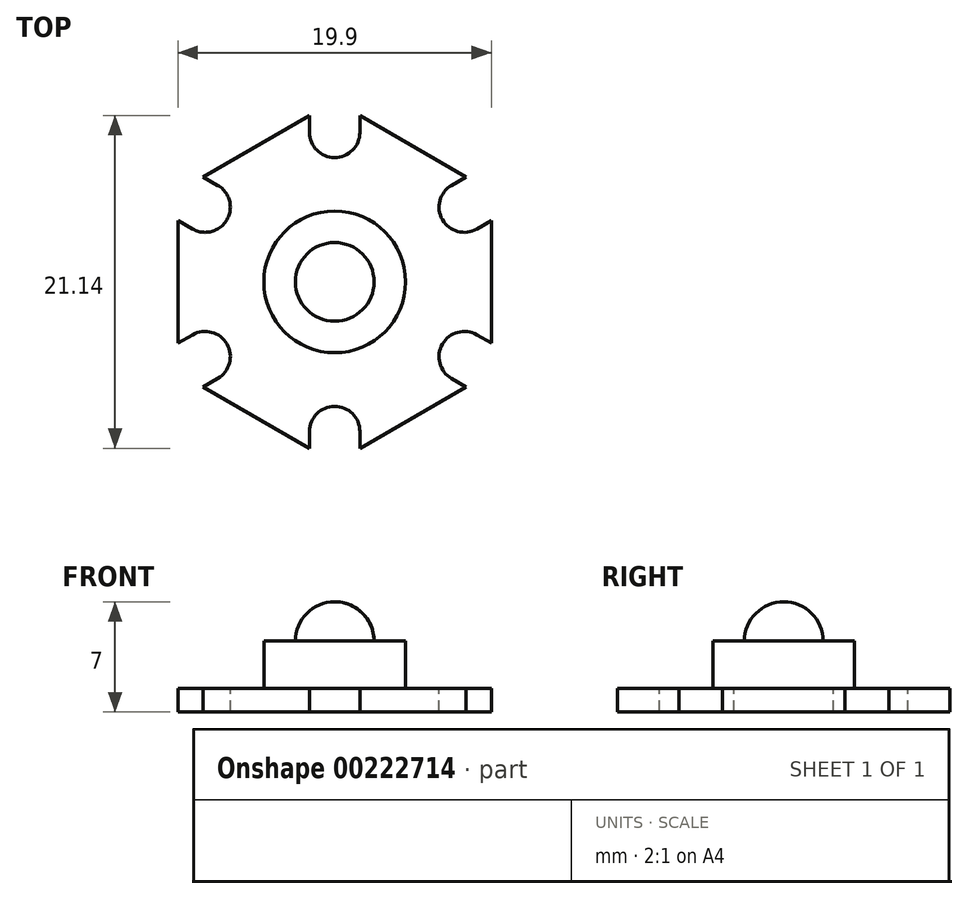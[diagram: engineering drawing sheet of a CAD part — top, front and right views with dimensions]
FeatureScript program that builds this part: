
annotation { "Feature Type Name" : "Feature", "Feature Type Description" : "" }
export const myFeature = defineFeature(function(context is Context, id is Id, definition is map)
    precondition{}
    {
        {
            var Q0;
            Q0=qCreatedBy(makeId("Top.planeOp"),FACE);
            var sketch = newSketch(context, id + "F0", { "sketchPlane" : qUnion([Q0])});
            skCircle(sketch, "E0.cCircle", {"center": v(0, 0) * mm, "radius": 9.95 * mm, "construction": true});
            skLineSegment(sketch, "E0.0", {"start": v(9.95, 5.74) * mm, "end": v(9.95, -5.74) * mm});
            skLineSegment(sketch, "E0.1", {"start": v(9.95, -5.74) * mm, "end": v(0, -11.49) * mm});
            skLineSegment(sketch, "E0.2", {"start": v(0, -11.49) * mm, "end": v(-9.95, -5.74) * mm});
            skLineSegment(sketch, "E0.3", {"start": v(-9.95, -5.74) * mm, "end": v(-9.95, 5.74) * mm});
            skLineSegment(sketch, "E0.4", {"start": v(-9.95, 5.74) * mm, "end": v(0, 11.49) * mm});
            skLineSegment(sketch, "E0.5", {"start": v(0, 11.49) * mm, "end": v(9.95, 5.74) * mm});
            skPoint(sketch, "E0.0.midPoint", {"position": v(9.95, 0) * mm});
            skSolve(sketch);
        }
        {
            var Q0;
            Q0=makeQuery(id+"F0.imprint","IMPRINT",FACE,{"disambiguationData":[TD([[makeQuery(id+"F0.imprint","IMPRINT",EDGE,{"derivedFrom":sQuery(id+"F0.wireOp",EDGE,"E0.0")}),-1.0]])]});
            extrude(context, id + "F1", {"entities" : qUnion([Q0]), "depth" : 1.5 * mm});
        }
        {
            var Q0;
            Q0=makeQuery(id+"F1.opExtrude","CAP_FACE",FACE,{"disambiguationData":[OSD([sQuery(id+"F0.wireOp",EDGE,"E0.0"),sQuery(id+"F0.wireOp",EDGE,"E0.1"),sQuery(id+"F0.wireOp",EDGE,"E0.2"),sQuery(id+"F0.wireOp",EDGE,"E0.3"),sQuery(id+"F0.wireOp",EDGE,"E0.4"),sQuery(id+"F0.wireOp",EDGE,"E0.5")])],"isStart":false});
            var sketch = newSketch(context, id + "F2", { "sketchPlane" : qUnion([Q0])});
            skLineSegment(sketch, "E1.0.0", {"start": v(9.95, 5.74) * mm, "end": v(0, 11.49) * mm, "construction": true});
            skLineSegment(sketch, "E1.0.1", {"start": v(0, 11.49) * mm, "end": v(-9.95, 5.74) * mm, "construction": true});
            skLineSegment(sketch, "E1.0.2", {"start": v(-9.95, 5.74) * mm, "end": v(-9.95, -5.74) * mm, "construction": true});
            skLineSegment(sketch, "E1.0.3", {"start": v(-9.95, -5.74) * mm, "end": v(0, -11.49) * mm, "construction": true});
            skLineSegment(sketch, "E1.0.4", {"start": v(0, -11.49) * mm, "end": v(9.95, -5.74) * mm, "construction": true});
            skLineSegment(sketch, "E1.0.5", {"start": v(9.95, -5.74) * mm, "end": v(9.95, 5.74) * mm, "construction": true});
            skLineSegment(sketch, "E2", {"start": v(0, 11.49) * mm, "end": v(0, -11.49) * mm, "construction": true});
            skArc(sketch, "E3", {"start": v(-1.6, 9.5) * mm, "mid": v(0, 7.9) * mm, "end": v(1.6, 9.5) * mm});
            skLineSegment(sketch, "E4", {"start": v(-1.6, 9.5) * mm, "end": v(1.6, 9.5) * mm, "construction": true});
            skLineSegment(sketch, "E5", {"start": v(-1.6, 9.5) * mm, "end": v(-1.6, 10.57) * mm});
            skLineSegment(sketch, "E6", {"start": v(1.6, 9.5) * mm, "end": v(1.6, 10.57) * mm});
            skLineSegment(sketch, "E7", {"start": v(-1.6, 10.57) * mm, "end": v(0, 11.49) * mm});
            skLineSegment(sketch, "E8", {"start": v(1.6, 10.57) * mm, "end": v(0, 11.49) * mm});
            skLineSegment(sketch, "E9.1.0", {"start": v(-7.43, 6.14) * mm, "end": v(-8.35, 6.67) * mm});
            skLineSegment(sketch, "E9.1.1", {"start": v(-9.03, 3.36) * mm, "end": v(-9.95, 3.9) * mm});
            skLineSegment(sketch, "E9.1.2", {"start": v(-9.03, 3.36) * mm, "end": v(-7.43, 6.14) * mm, "construction": true});
            skLineSegment(sketch, "E9.1.3", {"start": v(-8.35, 6.67) * mm, "end": v(-9.95, 5.74) * mm});
            skArc(sketch, "E9.1.4", {"start": v(-9.03, 3.36) * mm, "mid": v(-6.84, 3.95) * mm, "end": v(-7.43, 6.14) * mm});
            skLineSegment(sketch, "E9.1.5", {"start": v(-9.95, 3.9) * mm, "end": v(-9.95, 5.74) * mm});
            skLineSegment(sketch, "E9.2.0", {"start": v(-9.03, -3.36) * mm, "end": v(-9.95, -3.9) * mm});
            skLineSegment(sketch, "E9.2.1", {"start": v(-7.43, -6.14) * mm, "end": v(-8.35, -6.67) * mm});
            skLineSegment(sketch, "E9.2.2", {"start": v(-7.43, -6.14) * mm, "end": v(-9.03, -3.36) * mm, "construction": true});
            skLineSegment(sketch, "E9.2.3", {"start": v(-9.95, -3.9) * mm, "end": v(-9.95, -5.74) * mm});
            skArc(sketch, "E9.2.4", {"start": v(-7.43, -6.14) * mm, "mid": v(-6.84, -3.95) * mm, "end": v(-9.03, -3.36) * mm});
            skLineSegment(sketch, "E9.2.5", {"start": v(-8.35, -6.67) * mm, "end": v(-9.95, -5.74) * mm});
            skLineSegment(sketch, "E9.3.0", {"start": v(-1.6, -9.5) * mm, "end": v(-1.6, -10.57) * mm});
            skLineSegment(sketch, "E9.3.1", {"start": v(1.6, -9.5) * mm, "end": v(1.6, -10.57) * mm});
            skLineSegment(sketch, "E9.3.2", {"start": v(1.6, -9.5) * mm, "end": v(-1.6, -9.5) * mm, "construction": true});
            skLineSegment(sketch, "E9.3.3", {"start": v(-1.6, -10.57) * mm, "end": v(0, -11.49) * mm});
            skArc(sketch, "E9.3.4", {"start": v(1.6, -9.5) * mm, "mid": v(0, -7.9) * mm, "end": v(-1.6, -9.5) * mm});
            skLineSegment(sketch, "E9.3.5", {"start": v(1.6, -10.57) * mm, "end": v(0, -11.49) * mm});
            skLineSegment(sketch, "E9.4.0", {"start": v(7.43, -6.14) * mm, "end": v(8.35, -6.67) * mm});
            skLineSegment(sketch, "E9.4.1", {"start": v(9.03, -3.36) * mm, "end": v(9.95, -3.9) * mm});
            skLineSegment(sketch, "E9.4.2", {"start": v(9.03, -3.36) * mm, "end": v(7.43, -6.14) * mm, "construction": true});
            skLineSegment(sketch, "E9.4.3", {"start": v(8.35, -6.67) * mm, "end": v(9.95, -5.74) * mm});
            skArc(sketch, "E9.4.4", {"start": v(9.03, -3.36) * mm, "mid": v(6.84, -3.95) * mm, "end": v(7.43, -6.14) * mm});
            skLineSegment(sketch, "E9.4.5", {"start": v(9.95, -3.9) * mm, "end": v(9.95, -5.74) * mm});
            skLineSegment(sketch, "E9.5.0", {"start": v(9.03, 3.36) * mm, "end": v(9.95, 3.9) * mm});
            skLineSegment(sketch, "E9.5.1", {"start": v(7.43, 6.14) * mm, "end": v(8.35, 6.67) * mm});
            skLineSegment(sketch, "E9.5.2", {"start": v(7.43, 6.14) * mm, "end": v(9.03, 3.36) * mm, "construction": true});
            skLineSegment(sketch, "E9.5.3", {"start": v(9.95, 3.9) * mm, "end": v(9.95, 5.74) * mm});
            skArc(sketch, "E9.5.4", {"start": v(7.43, 6.14) * mm, "mid": v(6.84, 3.95) * mm, "end": v(9.03, 3.36) * mm});
            skLineSegment(sketch, "E9.5.5", {"start": v(8.35, 6.67) * mm, "end": v(9.95, 5.74) * mm});
            skPoint(sketch, "E9.center", {"position": v(0, 0) * mm});
            skSolve(sketch);
        }
        {
            var Q0;
            Q0=makeQuery(id+"F2.imprint","IMPRINT",FACE,{"disambiguationData":[TD([[makeQuery(id+"F2.imprint","IMPRINT",EDGE,{"derivedFrom":sQuery(id+"F2.wireOp",EDGE,"E3")}),1.0]])]});
            var Q1;
            Q1=makeQuery(id+"F2.imprint","IMPRINT",FACE,{"disambiguationData":[TD([[makeQuery(id+"F2.imprint","IMPRINT",EDGE,{"derivedFrom":sQuery(id+"F2.wireOp",EDGE,"E9.5.0")}),1.0]])]});
            var Q2;
            Q2=makeQuery(id+"F2.imprint","IMPRINT",FACE,{"disambiguationData":[TD([[makeQuery(id+"F2.imprint","IMPRINT",EDGE,{"derivedFrom":sQuery(id+"F2.wireOp",EDGE,"E9.4.0")}),1.0]])]});
            var Q3;
            Q3=makeQuery(id+"F2.imprint","IMPRINT",FACE,{"disambiguationData":[TD([[makeQuery(id+"F2.imprint","IMPRINT",EDGE,{"derivedFrom":sQuery(id+"F2.wireOp",EDGE,"E9.2.0")}),1.0]])]});
            var Q4;
            Q4=makeQuery(id+"F2.imprint","IMPRINT",FACE,{"disambiguationData":[TD([[makeQuery(id+"F2.imprint","IMPRINT",EDGE,{"derivedFrom":sQuery(id+"F2.wireOp",EDGE,"E9.1.0")}),1.0]])]});
            var Q5;
            Q5=makeQuery(id+"F2.imprint","IMPRINT",FACE,{"disambiguationData":[TD([[makeQuery(id+"F2.imprint","IMPRINT",EDGE,{"derivedFrom":sQuery(id+"F2.wireOp",EDGE,"E9.3.0")}),1.0]])]});
            extrude(context, id + "F3", {"entities" : qUnion([Q0, Q1, Q2, Q3, Q4, Q5]), "operationType" : NewBodyOperationType.REMOVE, "endBound" : BoundingType.THROUGH_ALL, "oppositeDirection" : true, "depth" : 25 * mm});
        }
        {
            var Q0;
            Q0=makeQuery(id+"F1.opExtrude","CAP_FACE",FACE,{"disambiguationData":[OSD([sQuery(id+"F0.wireOp",EDGE,"E0.0"),sQuery(id+"F0.wireOp",EDGE,"E0.1"),sQuery(id+"F0.wireOp",EDGE,"E0.2"),sQuery(id+"F0.wireOp",EDGE,"E0.3"),sQuery(id+"F0.wireOp",EDGE,"E0.4"),sQuery(id+"F0.wireOp",EDGE,"E0.5")])],"isStart":false});
            var sketch = newSketch(context, id + "F4", { "sketchPlane" : qUnion([Q0])});
            skCircle(sketch, "E10", {"center": v(0, 0) * mm, "radius": 4.5 * mm});
            skSolve(sketch);
        }
        {
            var Q0;
            Q0=makeQuery(id+"F4.imprint","IMPRINT",FACE,{"disambiguationData":[TD([[makeQuery(id+"F4.imprint","IMPRINT",EDGE,{"derivedFrom":sQuery(id+"F4.wireOp",EDGE,"E10")}),1.0]])]});
            extrude(context, id + "F5", {"entities" : qUnion([Q0]), "operationType" : NewBodyOperationType.ADD, "depth" : 3 * mm});
        }
        {
            var Q0;
            Q0=makeQuery(id+"F5.opExtrude","CAP_FACE",FACE,{"disambiguationData":[OSD([sQuery(id+"F4.wireOp",EDGE,"E10")])],"isStart":false});
            var sketch = newSketch(context, id + "F6", { "sketchPlane" : qUnion([Q0])});
            skCircle(sketch, "E11", {"center": v(0, 0) * mm, "radius": 2.5 * mm});
            skSolve(sketch);
        }
        {
            var Q0;
            Q0=makeQuery(id+"F6.imprint","IMPRINT",FACE,{"disambiguationData":[TD([[makeQuery(id+"F6.imprint","IMPRINT",EDGE,{"derivedFrom":sQuery(id+"F6.wireOp",EDGE,"E11")}),1.0]])]});
            extrude(context, id + "F7", {"entities" : qUnion([Q0]), "operationType" : NewBodyOperationType.ADD, "depth" : 2.5 * mm});
        }
        {
            var Q0;
            Q0=makeQuery(id+"F7.opExtrude","CAP_EDGE",EDGE,{"disambiguationData":[OSD([sQuery(id+"F6.wireOp",EDGE,"E11")])],"isStart":false});
            fillet(context, id + "F8", {"entities" : qUnion([Q0]), "radius" : 2.5 * mm, "tangentPropagation" : true, "allowEdgeOverflow" : false});
        }
    });
